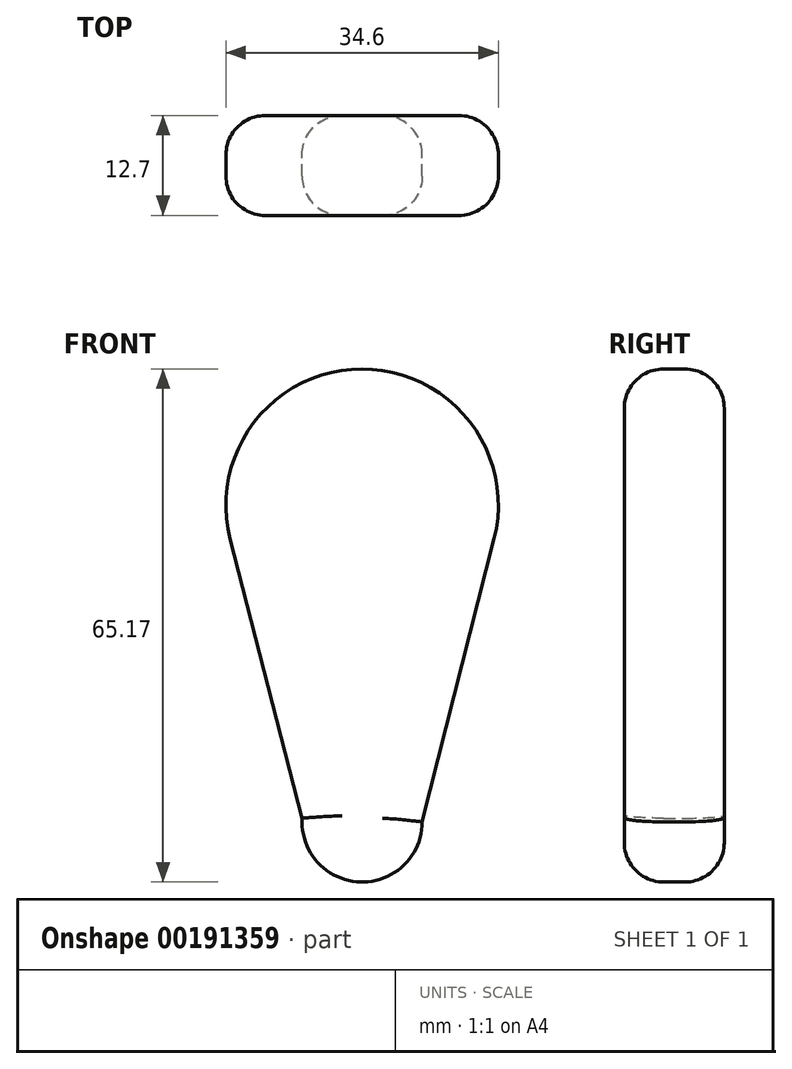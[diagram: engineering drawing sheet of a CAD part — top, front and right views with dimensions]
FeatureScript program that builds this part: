
annotation { "Feature Type Name" : "Feature", "Feature Type Description" : "" }
export const myFeature = defineFeature(function(context is Context, id is Id, definition is map)
    precondition{}
    {
        {
            var Q0;
            Q0=qCreatedBy(makeId("Front.planeOp"),FACE);
            var sketch = newSketch(context, id + "F0", { "sketchPlane" : qUnion([Q0])});
            skArc(sketch, "E0", {"start": v(16.77, 35.98) * mm, "mid": v(-0.03, 57.54) * mm, "end": v(-16.76, 35.92) * mm});
            skLineSegment(sketch, "E1", {"start": v(7.63, 0) * mm, "end": v(16.77, 35.98) * mm});
            skLineSegment(sketch, "E2", {"start": v(-16.76, 35.92) * mm, "end": v(-7.5, 0) * mm});
            skArc(sketch, "E3", {"start": v(-7.62, 0.46) * mm, "mid": v(-0.23, -7.63) * mm, "end": v(7.63, 0) * mm});
            skSolve(sketch);
        }
        {
            var Q0;
            {var subQ0=sQuery(id+"F0.wireOp",EDGE,"E0");Q0=makeQuery(id+"F0.imprint","IMPRINT",FACE,{"disambiguationData":[TD([[makeQuery(id+"F0.imprint","IMPRINT",EDGE,{"derivedFrom":subQ0}),1.0]])]});}
            extrude(context, id + "F1", {"entities" : qUnion([Q0]), "endBound" : BoundingType.SYMMETRIC, "depth" : 12.7 * mm});
        }
        {
            var Q0;
            Q0=makeQuery(id+"F1.opExtrude","CAP_EDGE",EDGE,{"disambiguationData":[OSD([sQuery(id+"F0.wireOp",EDGE,"E0")])],"isStart":true});
            var Q1;
            Q1=makeQuery(id+"F1.opExtrude","CAP_EDGE",EDGE,{"disambiguationData":[OSD([sQuery(id+"F0.wireOp",EDGE,"E1")])],"isStart":true});
            var Q2;
            Q2=makeQuery(id+"F1.opExtrude","CAP_EDGE",EDGE,{"disambiguationData":[OSD([sQuery(id+"F0.wireOp",EDGE,"E3")])],"isStart":true});
            var Q3;
            Q3=makeQuery(id+"F1.opExtrude","CAP_EDGE",EDGE,{"disambiguationData":[OSD([sQuery(id+"F0.wireOp",EDGE,"E2")])],"isStart":true});
            var Q4;
            Q4=makeQuery(id+"F1.opExtrude","CAP_EDGE",EDGE,{"disambiguationData":[OSD([sQuery(id+"F0.wireOp",EDGE,"E0")])],"isStart":false});
            var Q5;
            Q5=makeQuery(id+"F1.opExtrude","CAP_EDGE",EDGE,{"disambiguationData":[OSD([sQuery(id+"F0.wireOp",EDGE,"E2")])],"isStart":false});
            var Q6;
            Q6=makeQuery(id+"F1.opExtrude","CAP_EDGE",EDGE,{"disambiguationData":[OSD([sQuery(id+"F0.wireOp",EDGE,"E3")])],"isStart":false});
            fillet(context, id + "F2", {"entities" : qUnion([Q0, Q1, Q2, Q3, Q4, Q5, Q6]), "radius" : 5 * mm, "tangentPropagation" : true, "allowEdgeOverflow" : false});
        }
    });
